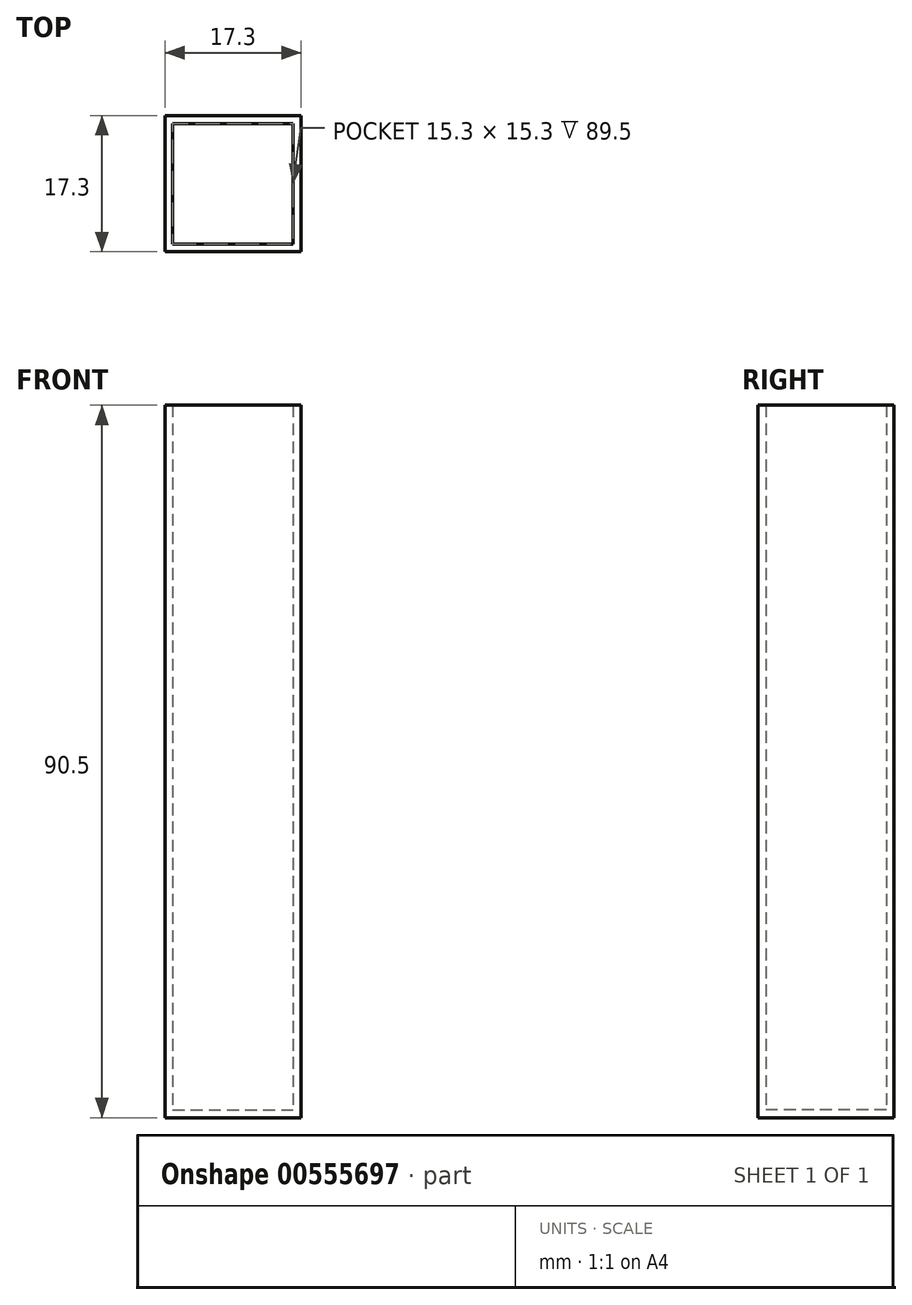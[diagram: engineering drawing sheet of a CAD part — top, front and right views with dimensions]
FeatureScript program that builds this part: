
annotation { "Feature Type Name" : "Feature", "Feature Type Description" : "" }
export const myFeature = defineFeature(function(context is Context, id is Id, definition is map)
    precondition{}
    {
        {
            var Q0;
            Q0=qCreatedBy(makeId("Top.planeOp"),FACE);
            var sketch = newSketch(context, id + "F0", { "sketchPlane" : qUnion([Q0])});
            skLineSegment(sketch, "E0.bottom", {"start": v(-8.65, 8.65) * mm, "end": v(8.65, 8.65) * mm});
            skLineSegment(sketch, "E0.top", {"start": v(-8.65, -8.65) * mm, "end": v(8.65, -8.65) * mm});
            skLineSegment(sketch, "E0.left", {"start": v(-8.65, 8.65) * mm, "end": v(-8.65, -8.65) * mm});
            skLineSegment(sketch, "E0.right", {"start": v(8.65, 8.65) * mm, "end": v(8.65, -8.65) * mm});
            skLineSegment(sketch, "E1", {"start": v(-8.65, 8.65) * mm, "end": v(8.65, -8.65) * mm, "construction": true});
            skPoint(sketch, "E2", {"position": v(0, 0) * mm});
            skSolve(sketch);
        }
        {
            var Q0;
            Q0=makeQuery(id+"F0.imprint","IMPRINT",FACE,{"disambiguationData":[TD([[makeQuery(id+"F0.imprint","IMPRINT",EDGE,{"derivedFrom":sQuery(id+"F0.wireOp",EDGE,"E0.bottom")}),-1.0]])]});
            extrude(context, id + "F1", {"entities" : qUnion([Q0]), "depth" : 90.5 * mm, "offsetDistance" : 25 * mm});
        }
        {
            var Q0;
            Q0=makeQuery(id+"F1.opExtrude","CAP_FACE",FACE,{"disambiguationData":[OSD([sQuery(id+"F0.wireOp",EDGE,"E0.bottom"),sQuery(id+"F0.wireOp",EDGE,"E0.top"),sQuery(id+"F0.wireOp",EDGE,"E0.left"),sQuery(id+"F0.wireOp",EDGE,"E0.right")])],"isStart":false});
            shell(context, id + "F2", {"entities" : qUnion([Q0]), "thickness" : 1 * mm});
        }
    });
